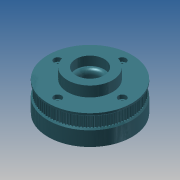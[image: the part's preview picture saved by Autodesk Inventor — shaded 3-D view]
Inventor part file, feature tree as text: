
AUTODESK INVENTOR PART (.ipt)
format: ipt  version: 2013 (Build 170138000, 138)  size: 1,281,536 bytes
history: native  units: mm
features: extrude x11, sketch x11, pattern_circular x2, chamfer x1, mirror x1, fillet x1
ambient origin geometry x8: Origin, YZ Plane, XZ Plane, XY Plane, X Axis, Y Axis, Z Axis, Center Point
bodies: Solid1 (feature_tree)
feature tree (27):
  extrude  "Extrusion1"  Depth=0.628319mm
  pattern_circular  "Circular Pattern1"  Count=100  [1 undecoded]
  extrude  "Extrusion3"  Depth=0.1mm
  chamfer  "Chamfer2"  Distance=2.5mm
  mirror  "Mirror1"
  extrude  "Extrusion7"  Depth=15.0mm
  extrude  "Extrusion8"  Depth=3.5mm
  extrude  "Extrusion9"  Depth=15.0mm
  extrude  "Extrusion10"  Depth=25.0mm
  extrude  "Extrusion11"  Depth=2.0mm TaperAngle=0.0deg
  pattern_circular  "Circular Pattern2"  [2 undecoded]
  extrude  "Extrusion12"  Depth=3.0mm TaperAngle=0.0deg
  fillet  "Fillet1"  Radius=22.0mm
  extrude  "Extrusion4"  Depth=7.0mm TaperAngle=0.0deg
  extrude  "Extrusion5"  Depth=1.0mm
  extrude  "Extrusion6"  Depth=35.0mm
  sketch  "Sketch1"  dims[d0=63.661977mm d9=0.628319mm]
  sketch  "Sketch3"  dims[d11=0.254mm]
  sketch  "Sketch4"  dims[d12=0.3mm]
  sketch  "Sketch5"  dims[d13=0.4mm]
  sketch  "Sketch6"  dims[d14=1.0mm]
  sketch  "Sketch7"  dims[d15=0.555mm]
  sketch  "Sketch8"  dims[d16=0.75mm]
  sketch  "Sketch9"  dims[d17=0.254mm]
  sketch  "Sketch10"  dims[d18=8.0mm d19=0.0mm d20=1000.0mm]
  sketch  "Sketch11"  dims[d21=360.0deg d23=0.1mm d32=2.5mm d33=0.0mm]
  sketch  "Sketch12"  dims[d34=1.0mm d35=2.0mm d36=45.0deg d37=15.0mm d39=3.5mm d40=15.0mm d41=25.0mm d42=2.0mm d43=0.0mm d44=6.0mm d46=3.0mm d47=0.0mm d49=22.0mm d51=7.0mm d52=0.0mm d53=1.0mm d54=35.0mm d56=8.0mm d57=0.0mm d58=15.0mm d60=10.0mm d61=0.0mm d62=22.0mm d64=7.0mm d65=0.0mm d68=25.0mm d69=3.5mm d70=7.0mm d71=0.0mm d72=6.0mm d74=3.0mm d75=0.0mm d76=40.0mm d77=360.0deg d80=9.7mm d81=0.0mm d82=3.5mm]
note: 3 required parameter values undecoded (feature->parameter linkage not recoverable at this tier; creation-order binding heuristic only, values carry confidence <= 0.55)
